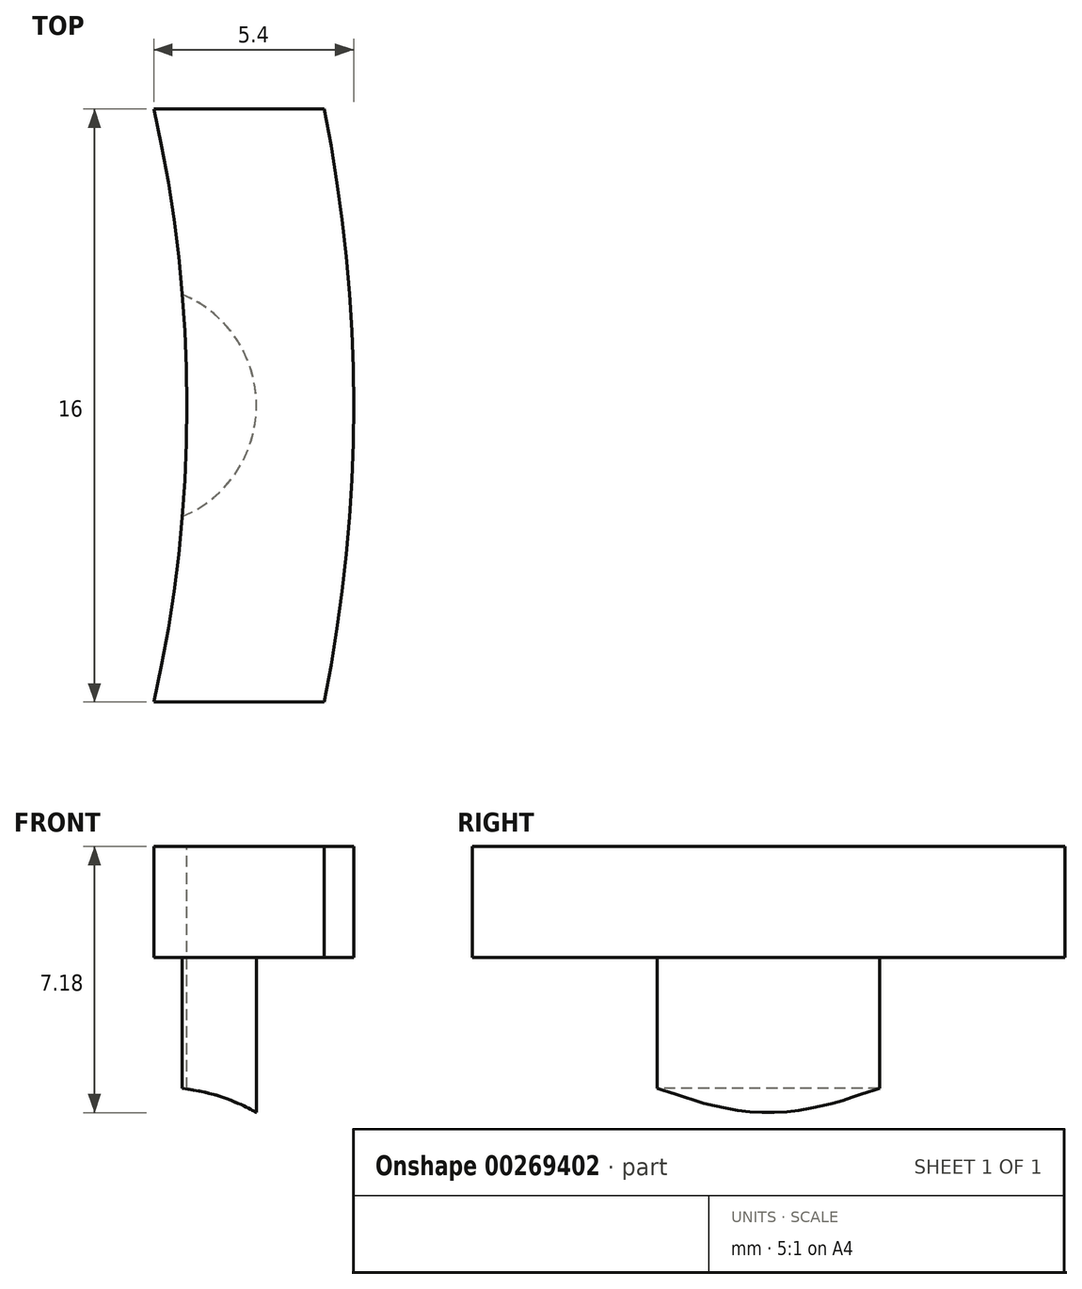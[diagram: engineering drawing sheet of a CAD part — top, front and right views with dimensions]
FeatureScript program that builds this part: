
annotation { "Feature Type Name" : "Feature", "Feature Type Description" : "" }
export const myFeature = defineFeature(function(context is Context, id is Id, definition is map)
    precondition{}
    {
        {
            var Q0;
            Q0=qCreatedBy(makeId("Top.planeOp"),FACE);
            var sketch = newSketch(context, id + "F0", { "sketchPlane" : qUnion([Q0])});
            skCircle(sketch, "E0", {"center": v(0, 0) * mm, "radius": 25.75 * mm});
            skCircle(sketch, "E1", {"center": v(0, 0) * mm, "radius": 40.5 * mm});
            skCircle(sketch, "E2", {"center": v(0, 0) * mm, "radius": 33 * mm});
            skCircle(sketch, "E3", {"center": v(0, 0) * mm, "radius": 36 * mm});
            skPoint(sketch, "E4", {"position": v(0, 50.94) * mm});
            skSolve(sketch);
        }
        {
            var Q0;
            Q0=makeQuery(id+"F0.imprint","IMPRINT",FACE,{"disambiguationData":[TD([[makeQuery(id+"F0.imprint","IMPRINT",EDGE,{"derivedFrom":sQuery(id+"F0.wireOp",EDGE,"E1")}),1.0]])]});
            var Q1;
            Q1=makeQuery(id+"F0.imprint","IMPRINT",FACE,{"disambiguationData":[TD([[makeQuery(id+"F0.imprint","IMPRINT",EDGE,{"derivedFrom":sQuery(id+"F0.wireOp",EDGE,"E0")}),-1.0]])]});
            extrude(context, id + "F1", {"entities" : qUnion([Q0, Q1]), "depth" : 16 * mm});
        }
        {
            var Q0;
            Q0=qCreatedBy(makeId("Right.planeOp"),FACE);
            var sketch = newSketch(context, id + "F2", { "sketchPlane" : qUnion([Q0])});
            skLineSegment(sketch, "E5", {"start": v(0, 0) * mm, "end": v(0, 16) * mm});
            skPoint(sketch, "E6", {"position": v(0, 8) * mm});
            skSolve(sketch);
        }
        {
            var Q0;
            Q0=makeQuery(id+"F1.opExtrude","CAP_FACE",FACE,{"disambiguationData":[OSD([sQuery(id+"F0.wireOp",EDGE,"E0"),sQuery(id+"F0.wireOp",EDGE,"E2")])],"isStart":false});
            var sketch = newSketch(context, id + "F3", { "sketchPlane" : qUnion([Q0])});
            skPoint(sketch, "E7", {"position": v(0, -33) * mm});
            skSolve(sketch);
        }
        {
            var Q0;
            Q0=qCreatedBy(makeId("Right.planeOp"),FACE);
            var sketch = newSketch(context, id + "F4", { "sketchPlane" : qUnion([Q0])});
            skCircle(sketch, "E8", {"center": v(-35.5, 8) * mm, "radius": 4.5 * mm});
            skPoint(sketch, "E9", {"position": v(-33.5, 8) * mm});
            skSolve(sketch);
        }
        {
            var Q0;
            Q0=qCreatedBy(makeId("Right.planeOp"),FACE);
            var sketch = newSketch(context, id + "F5", { "sketchPlane" : qUnion([Q0])});
            skLineSegment(sketch, "E10", {"start": v(-35.5, 11.25) * mm, "end": v(-35.5, 4.75) * mm});
            skPoint(sketch, "E11", {"position": v(0, 5) * mm});
            skPoint(sketch, "E12", {"position": v(-35.5, 8) * mm});
            skArc(sketch, "E13", {"start": v(-35.5, 11.25) * mm, "mid": v(-38.75, 8) * mm, "end": v(-35.5, 4.75) * mm});
            skSolve(sketch);
        }
        {
            var Q0;
            Q0=qCreatedBy(makeId("Top.planeOp"),FACE);
            cPlane(context, id + "F6", {"entities" : qUnion([Q0]), "cplaneType" : CPlaneType.OFFSET, "offset" : 5 * mm, "width" : 150 * mm, "height" : 150 * mm});
        }
        {
            var Q0;
            Q0=makeQuery(id+"F1.opExtrude","CAP_FACE",FACE,{"disambiguationData":[OSD([sQuery(id+"F0.wireOp",EDGE,"E1"),sQuery(id+"F0.wireOp",EDGE,"E3")])],"isStart":false});
            var sketch = newSketch(context, id + "F7", { "sketchPlane" : qUnion([Q0])});
            skCircle(sketch, "E14", {"center": v(34.62, 0) * mm, "radius": 3.25 * mm});
            skSolve(sketch);
        }
        {
            var Q0;
            Q0=makeQuery(id+"F7.imprint","IMPRINT",FACE,{"disambiguationData":[TD([[makeQuery(id+"F7.imprint","IMPRINT",EDGE,{"derivedFrom":sQuery(id+"F7.wireOp",EDGE,"E14")}),1.0]])]});
            extrude(context, id + "F8", {"entities" : qUnion([Q0]), "operationType" : NewBodyOperationType.REMOVE, "oppositeDirection" : true, "depth" : 8 * mm});
        }
        {
            var Q0;
            Q0=makeQuery(id+"F1.opExtrude","CAP_FACE",FACE,{"disambiguationData":[OSD([sQuery(id+"F0.wireOp",EDGE,"E1"),sQuery(id+"F0.wireOp",EDGE,"E3")])],"isStart":true});
            var sketch = newSketch(context, id + "F9", { "sketchPlane" : qUnion([Q0])});
            skPoint(sketch, "E15", {"position": v(0, 46) * mm});
            skCircle(sketch, "E16", {"center": v(0, 0) * mm, "radius": 51 * mm});
            skLineSegment(sketch, "E17", {"start": v(-5, 50.75) * mm, "end": v(-5, 35.65) * mm});
            skLineSegment(sketch, "E18", {"start": v(5, 50.75) * mm, "end": v(5, 35.65) * mm});
            skSolve(sketch);
        }
        {
            var Q0;
            {var subQ0=sQuery(id+"F9.wireOp",EDGE,"E17");var subQ1=makeQuery(id+"F1.opExtrude","CAP_EDGE",EDGE,{"disambiguationData":[OSD([sQuery(id+"F0.wireOp",EDGE,"E3")])],"isStart":true});var subQ2=makeQuery(id+"F9.imprint","INTERSECT",VERTEX,{"derivedFrom":[subQ1,subQ0]});Q0=makeQuery(id+"F9.imprint","IMPRINT",FACE,{"disambiguationData":[TD([[makeQuery(id+"F9.imprint","IMPRINT",EDGE,{"disambiguationData":[TD([[subQ2,1.0]])],"derivedFrom":subQ0}),1.0]])]});}
            var Q1;
            {var subQ0=sQuery(id+"F9.wireOp",EDGE,"E17");var subQ1=sQuery(id+"F9.wireOp",EDGE,"E16");var subQ2=makeQuery(id+"F9.imprint","INTERSECT",VERTEX,{"derivedFrom":[subQ1,subQ0]});Q1=makeQuery(id+"F9.imprint","IMPRINT",FACE,{"disambiguationData":[TD([[makeQuery(id+"F9.imprint","IMPRINT",EDGE,{"disambiguationData":[TD([[subQ2,1.0]])],"derivedFrom":subQ1}),1.0]])]});}
            extrude(context, id + "F10", {"entities" : qUnion([Q0, Q1]), "depth" : 4 * mm});
        }
        {
            var Q0;
            Q0=sQuery(id+"F9.wireOp",VERTEX,"E15");
            var Q1;
            Q1=makeQuery(id+"F10.opExtrude","SWEPT_BODY",BODY,{"disambiguationData":[OSD([sQuery(id+"F0.wireOp",EDGE,"E3"),sQuery(id+"F9.wireOp",EDGE,"E16"),sQuery(id+"F9.wireOp",EDGE,"E17"),sQuery(id+"F9.wireOp",EDGE,"E18")])]});
            hole(context, id + "F11", {"style" : HoleStyle.SIMPLE, "endStyle" : HoleEndStyle.THROUGH, "oppositeDirection" : true, "holeDiameter" : 4 * mm, "tappedDepth" : 12 * mm, "tapClearance" : 3, "locations" : qUnion([Q0]), "scope" : qUnion([Q1])});
        }
        {
            var Q0;
            Q0=makeQuery(id+"F10.opExtrude","SWEPT_BODY",BODY,{"disambiguationData":[OSD([sQuery(id+"F0.wireOp",EDGE,"E3"),sQuery(id+"F9.wireOp",EDGE,"E16"),sQuery(id+"F9.wireOp",EDGE,"E17"),sQuery(id+"F9.wireOp",EDGE,"E18")])]});
            var Q1;
            Q1=makeQuery(id+"F1.opExtrude","CAP_EDGE",EDGE,{"disambiguationData":[OSD([sQuery(id+"F0.wireOp",EDGE,"E1")])],"isStart":true});
            circularPattern(context, id + "F12", {"operationType" : NewBodyOperationType.ADD, "entities" : qUnion([Q0]), "axis" : qUnion([Q1]), "angle" : 360 * degree, "instanceCount" : 6, "equalSpace" : true});
        }
        {
            var Q0;
            {var subQ0=sQuery(id+"F9.wireOp",EDGE,"E17");Q0=makeQuery(id+"F12.boolean.opBoolean","SPLIT",EDGE,{"disambiguationData":[topologyDisambiguationEdgeConnected([makeQuery(id+"F1.opExtrude","CAP_FACE",FACE,{"disambiguationData":[OSD([sQuery(id+"F0.wireOp",EDGE,"E1"),sQuery(id+"F0.wireOp",EDGE,"E3")])],"isStart":true})])],"derivedFrom":makeQuery(id+"F12.opPattern","COPY",EDGE,{"derivedFrom":makeQuery(id+"F10.opExtrude","CAP_EDGE",EDGE,{"disambiguationData":[OSD([subQ0])],"isStart":true}),"instanceName":"5"})});}
            var Q1;
            {var subQ0=sQuery(id+"F9.wireOp",EDGE,"E18");Q1=makeQuery(id+"F12.boolean.opBoolean","SPLIT",EDGE,{"disambiguationData":[topologyDisambiguationEdgeConnected([makeQuery(id+"F1.opExtrude","CAP_FACE",FACE,{"disambiguationData":[OSD([sQuery(id+"F0.wireOp",EDGE,"E1"),sQuery(id+"F0.wireOp",EDGE,"E3")])],"isStart":true})])],"derivedFrom":makeQuery(id+"F12.opPattern","COPY",EDGE,{"derivedFrom":makeQuery(id+"F10.opExtrude","CAP_EDGE",EDGE,{"disambiguationData":[OSD([subQ0])],"isStart":true}),"instanceName":"4"})});}
            var Q2;
            {var subQ0=sQuery(id+"F9.wireOp",EDGE,"E18");Q2=makeQuery(id+"F12.boolean.opBoolean","SPLIT",EDGE,{"disambiguationData":[topologyDisambiguationEdgeConnected([makeQuery(id+"F1.opExtrude","CAP_FACE",FACE,{"disambiguationData":[OSD([sQuery(id+"F0.wireOp",EDGE,"E1"),sQuery(id+"F0.wireOp",EDGE,"E3")])],"isStart":true})])],"derivedFrom":makeQuery(id+"F12.opPattern","COPY",EDGE,{"derivedFrom":makeQuery(id+"F10.opExtrude","CAP_EDGE",EDGE,{"disambiguationData":[OSD([subQ0])],"isStart":true}),"instanceName":"3"})});}
            var Q3;
            {var subQ0=sQuery(id+"F9.wireOp",EDGE,"E17");Q3=makeQuery(id+"F12.boolean.opBoolean","SPLIT",EDGE,{"disambiguationData":[topologyDisambiguationEdgeConnected([makeQuery(id+"F1.opExtrude","CAP_FACE",FACE,{"disambiguationData":[OSD([sQuery(id+"F0.wireOp",EDGE,"E1"),sQuery(id+"F0.wireOp",EDGE,"E3")])],"isStart":true})])],"derivedFrom":makeQuery(id+"F12.opPattern","COPY",EDGE,{"derivedFrom":makeQuery(id+"F10.opExtrude","CAP_EDGE",EDGE,{"disambiguationData":[OSD([subQ0])],"isStart":true}),"instanceName":"4"})});}
            var Q4;
            {var subQ0=sQuery(id+"F9.wireOp",EDGE,"E17");Q4=makeQuery(id+"F12.boolean.opBoolean","SPLIT",EDGE,{"disambiguationData":[topologyDisambiguationEdgeConnected([makeQuery(id+"F1.opExtrude","CAP_FACE",FACE,{"disambiguationData":[OSD([sQuery(id+"F0.wireOp",EDGE,"E1"),sQuery(id+"F0.wireOp",EDGE,"E3")])],"isStart":true})])],"derivedFrom":makeQuery(id+"F12.opPattern","COPY",EDGE,{"derivedFrom":makeQuery(id+"F10.opExtrude","CAP_EDGE",EDGE,{"disambiguationData":[OSD([subQ0])],"isStart":true}),"instanceName":"3"})});}
            var Q5;
            {var subQ0=sQuery(id+"F9.wireOp",EDGE,"E18");Q5=makeQuery(id+"F12.boolean.opBoolean","SPLIT",EDGE,{"disambiguationData":[topologyDisambiguationEdgeConnected([makeQuery(id+"F1.opExtrude","CAP_FACE",FACE,{"disambiguationData":[OSD([sQuery(id+"F0.wireOp",EDGE,"E1"),sQuery(id+"F0.wireOp",EDGE,"E3")])],"isStart":true})])],"derivedFrom":makeQuery(id+"F12.opPattern","COPY",EDGE,{"derivedFrom":makeQuery(id+"F10.opExtrude","CAP_EDGE",EDGE,{"disambiguationData":[OSD([subQ0])],"isStart":true}),"instanceName":"2"})});}
            var Q6;
            {var subQ0=sQuery(id+"F9.wireOp",EDGE,"E18");Q6=makeQuery(id+"F12.boolean.opBoolean","SPLIT",EDGE,{"disambiguationData":[topologyDisambiguationEdgeConnected([makeQuery(id+"F1.opExtrude","CAP_FACE",FACE,{"disambiguationData":[OSD([sQuery(id+"F0.wireOp",EDGE,"E1"),sQuery(id+"F0.wireOp",EDGE,"E3")])],"isStart":true})])],"derivedFrom":makeQuery(id+"F12.opPattern","COPY",EDGE,{"derivedFrom":makeQuery(id+"F10.opExtrude","CAP_EDGE",EDGE,{"disambiguationData":[OSD([subQ0])],"isStart":true}),"instanceName":"1"})});}
            var Q7;
            {var subQ0=sQuery(id+"F9.wireOp",EDGE,"E17");Q7=makeQuery(id+"F12.boolean.opBoolean","SPLIT",EDGE,{"disambiguationData":[topologyDisambiguationEdgeConnected([makeQuery(id+"F1.opExtrude","CAP_FACE",FACE,{"disambiguationData":[OSD([sQuery(id+"F0.wireOp",EDGE,"E1"),sQuery(id+"F0.wireOp",EDGE,"E3")])],"isStart":true})])],"derivedFrom":makeQuery(id+"F12.opPattern","COPY",EDGE,{"derivedFrom":makeQuery(id+"F10.opExtrude","CAP_EDGE",EDGE,{"disambiguationData":[OSD([subQ0])],"isStart":true}),"instanceName":"2"})});}
            var Q8;
            {var subQ0=sQuery(id+"F9.wireOp",EDGE,"E17");Q8=makeQuery(id+"F12.boolean.opBoolean","SPLIT",EDGE,{"disambiguationData":[topologyDisambiguationEdgeConnected([makeQuery(id+"F1.opExtrude","CAP_FACE",FACE,{"disambiguationData":[OSD([sQuery(id+"F0.wireOp",EDGE,"E1"),sQuery(id+"F0.wireOp",EDGE,"E3")])],"isStart":true})])],"derivedFrom":makeQuery(id+"F12.opPattern","COPY",EDGE,{"derivedFrom":makeQuery(id+"F10.opExtrude","CAP_EDGE",EDGE,{"disambiguationData":[OSD([subQ0])],"isStart":true}),"instanceName":"1"})});}
            var Q9;
            {var subQ0=sQuery(id+"F9.wireOp",EDGE,"E18");Q9=makeQuery(id+"F12.boolean.opBoolean","SPLIT",EDGE,{"disambiguationData":[topologyDisambiguationEdgeConnected([makeQuery(id+"F1.opExtrude","CAP_FACE",FACE,{"disambiguationData":[OSD([sQuery(id+"F0.wireOp",EDGE,"E1"),sQuery(id+"F0.wireOp",EDGE,"E3")])],"isStart":true})])],"derivedFrom":makeQuery(id+"F10.opExtrude","CAP_EDGE",EDGE,{"disambiguationData":[OSD([subQ0])],"isStart":true})});}
            var Q10;
            {var subQ0=sQuery(id+"F9.wireOp",EDGE,"E17");Q10=makeQuery(id+"F12.boolean.opBoolean","SPLIT",EDGE,{"disambiguationData":[topologyDisambiguationEdgeConnected([makeQuery(id+"F1.opExtrude","CAP_FACE",FACE,{"disambiguationData":[OSD([sQuery(id+"F0.wireOp",EDGE,"E1"),sQuery(id+"F0.wireOp",EDGE,"E3")])],"isStart":true})])],"derivedFrom":makeQuery(id+"F10.opExtrude","CAP_EDGE",EDGE,{"disambiguationData":[OSD([subQ0])],"isStart":true})});}
            var Q11;
            {var subQ0=sQuery(id+"F9.wireOp",EDGE,"E18");Q11=makeQuery(id+"F12.boolean.opBoolean","SPLIT",EDGE,{"disambiguationData":[topologyDisambiguationEdgeConnected([makeQuery(id+"F1.opExtrude","CAP_FACE",FACE,{"disambiguationData":[OSD([sQuery(id+"F0.wireOp",EDGE,"E1"),sQuery(id+"F0.wireOp",EDGE,"E3")])],"isStart":true})])],"derivedFrom":makeQuery(id+"F12.opPattern","COPY",EDGE,{"derivedFrom":makeQuery(id+"F10.opExtrude","CAP_EDGE",EDGE,{"disambiguationData":[OSD([subQ0])],"isStart":true}),"instanceName":"5"})});}
            fillet(context, id + "F13", {"entities" : qUnion([Q0, Q1, Q2, Q3, Q4, Q5, Q6, Q7, Q8, Q9, Q10, Q11]), "radius" : 5 * mm, "tangentPropagation" : true, "allowEdgeOverflow" : false});
        }
        {
            var Q0;
            {var subQ0=sQuery(id+"F7.wireOp",EDGE,"E14");var subQ1=makeQuery(id+"F1.opExtrude","CAP_EDGE",EDGE,{"disambiguationData":[OSD([sQuery(id+"F0.wireOp",EDGE,"E3")])],"isStart":false});var subQ2=makeQuery(id+"F7.imprint","INTERSECT",VERTEX,{"disambiguationData":[OD(0.0)],"derivedFrom":[subQ1,subQ0]});Q0=makeQuery(id+"F7.imprint","IMPRINT",FACE,{"disambiguationData":[TD([[makeQuery(id+"F7.imprint","IMPRINT",EDGE,{"disambiguationData":[TD([[subQ2,-1.0]])],"derivedFrom":subQ0}),1.0]])]});}
            extrude(context, id + "F14", {"entities" : qUnion([Q0]), "oppositeDirection" : true, "depth" : 5 * mm});
        }
        {
            var Q0;
            Q0=makeQuery(id+"F4.imprint","IMPRINT",FACE,{"disambiguationData":[TD([[makeQuery(id+"F4.imprint","IMPRINT",EDGE,{"derivedFrom":sQuery(id+"F4.wireOp",EDGE,"E8")}),1.0]])]});
            var Q1;
            Q1=makeQuery(id+"F1.opExtrude","SWEPT_FACE",FACE,{"disambiguationData":[OSD([sQuery(id+"F0.wireOp",EDGE,"E2")])]});
            revolve(context, id + "F15", {"operationType" : NewBodyOperationType.REMOVE, "entities" : qUnion([Q0]), "axis" : qUnion([Q1]), "revolveType" : RevolveType.FULL, "oppositeDirection" : true});
        }
        {
            var Q0;
            Q0=makeQuery(id+"F1.opExtrude","SWEPT_BODY",BODY,{"disambiguationData":[OSD([sQuery(id+"F0.wireOp",EDGE,"E0"),sQuery(id+"F0.wireOp",EDGE,"E2")])]});
            deleteBodies(context, id + "F16", {"entities" : qUnion([Q0])});
        }
        {
            var Q0;
            Q0=makeQuery(id+"F14.opExtrude","CAP_FACE",FACE,{"disambiguationData":[OSD([sQuery(id+"F0.wireOp",EDGE,"E3"),sQuery(id+"F7.wireOp",EDGE,"E14")])],"isStart":true});
            var sketch = newSketch(context, id + "F17", { "sketchPlane" : qUnion([Q0])});
            skCircle(sketch, "E19", {"center": v(0, 0) * mm, "radius": 40.5 * mm});
            skCircle(sketch, "E20", {"center": v(0, 0) * mm, "radius": 36 * mm});
            skLineSegment(sketch, "E21", {"start": v(35.1, -8) * mm, "end": v(39.7, -8) * mm});
            skLineSegment(sketch, "E22", {"start": v(35.1, 8) * mm, "end": v(39.7, 8) * mm});
            skSolve(sketch);
        }
        {
            var Q0;
            Q0=makeQuery(id+"F1.opExtrude","SWEPT_BODY",BODY,{"disambiguationData":[OSD([sQuery(id+"F0.wireOp",EDGE,"E1"),sQuery(id+"F0.wireOp",EDGE,"E3")])]});
            deleteBodies(context, id + "F18", {"entities" : qUnion([Q0])});
        }
        {
            var Q0;
            {var subQ1=makeQuery(id+"F14.opExtrude","CAP_EDGE",EDGE,{"disambiguationData":[OSD([sQuery(id+"F7.wireOp",EDGE,"E14")])],"isStart":true});Q0=makeQuery(id+"F17.imprint","IMPRINT",FACE,{"disambiguationData":[TD([[makeQuery(id+"F17.imprint","IMPRINT",EDGE,{"derivedFrom":subQ1}),1.0]])]});}
            var Q1;
            {var subQ0=sQuery(id+"F17.wireOp",EDGE,"E21");Q1=makeQuery(id+"F17.imprint","IMPRINT",FACE,{"disambiguationData":[TD([[makeQuery(id+"F17.imprint","IMPRINT",EDGE,{"derivedFrom":subQ0}),1.0]])]});}
            extrude(context, id + "F19", {"entities" : qUnion([Q0, Q1]), "operationType" : NewBodyOperationType.ADD, "depth" : 3 * mm});
        }
    });
